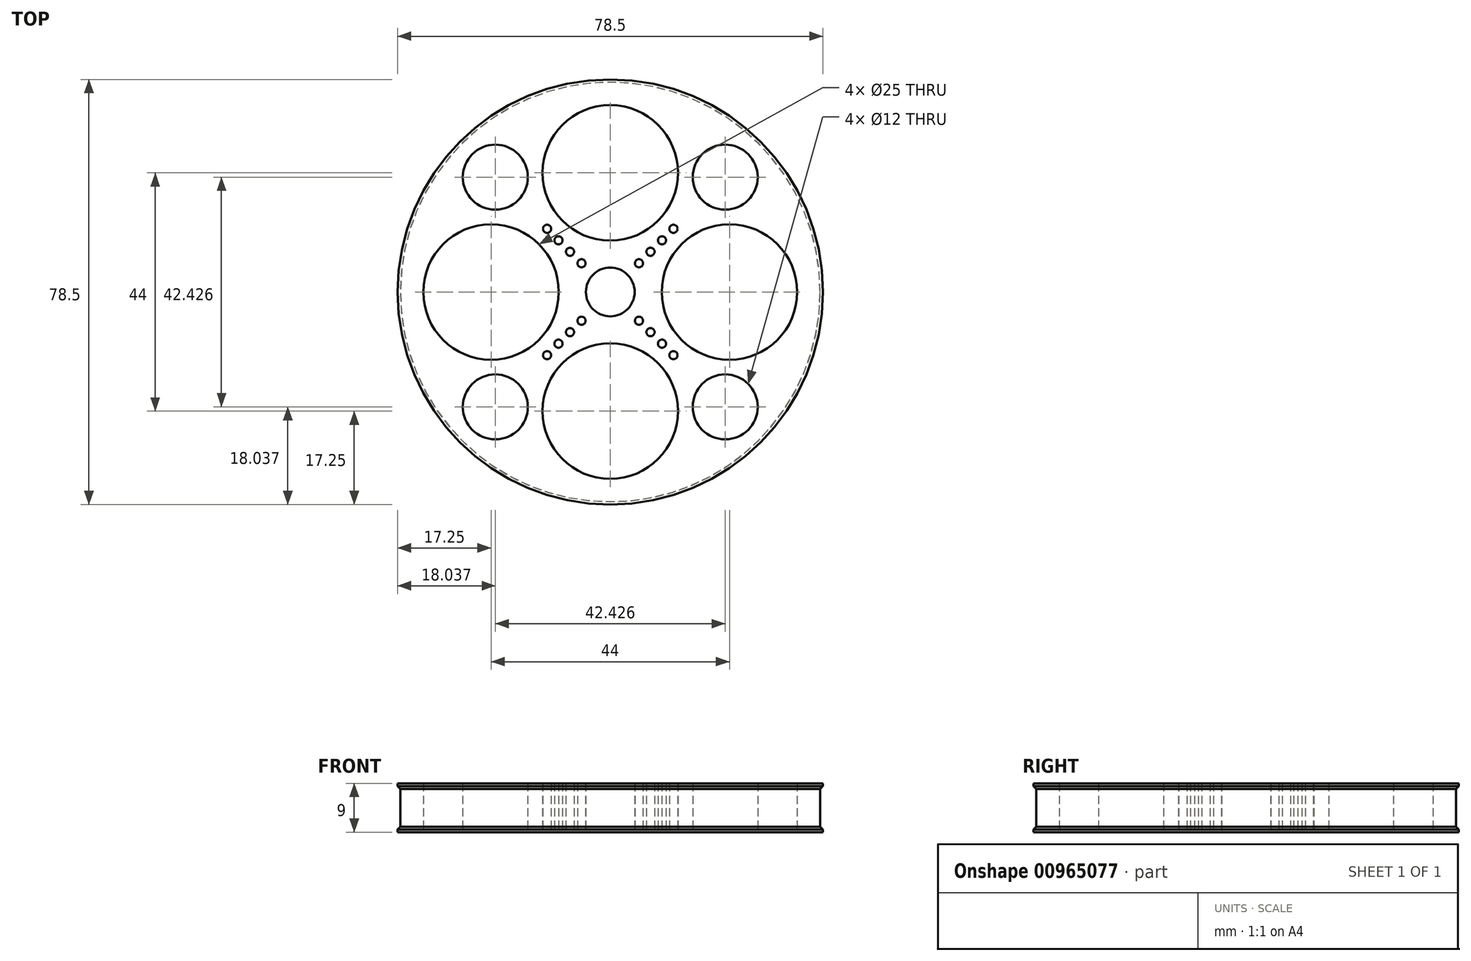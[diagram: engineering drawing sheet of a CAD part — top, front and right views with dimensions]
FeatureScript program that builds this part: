
annotation { "Feature Type Name" : "Feature", "Feature Type Description" : "" }
export const myFeature = defineFeature(function(context is Context, id is Id, definition is map)
    precondition{}
    {
        {
            var Q0;
            Q0=qCreatedBy(makeId("Top.planeOp"),FACE);
            var sketch = newSketch(context, id + "F0", { "sketchPlane" : qUnion([Q0])});
            skCircle(sketch, "E0", {"center": v(0, 0) * mm, "radius": 38.71 * mm});
            skCircle(sketch, "E1", {"center": v(0, 0) * mm, "radius": 4.5 * mm});
            skCircle(sketch, "E2", {"center": v(0, 22) * mm, "radius": 12.5 * mm});
            skCircle(sketch, "E3", {"center": v(22, 0) * mm, "radius": 12.5 * mm});
            skCircle(sketch, "E4", {"center": v(0, -22) * mm, "radius": 12.5 * mm});
            skCircle(sketch, "E5", {"center": v(-22, 0) * mm, "radius": 12.5 * mm});
            skLineSegment(sketch, "E6", {"start": v(0, 0) * mm, "end": v(36.46, 36.46) * mm, "construction": true});
            skLineSegment(sketch, "E7", {"start": v(0, 0) * mm, "end": v(-38.26, -38.26) * mm, "construction": true});
            skLineSegment(sketch, "E8", {"start": v(0, 0) * mm, "end": v(36.23, -36.23) * mm, "construction": true});
            skLineSegment(sketch, "E9", {"start": v(0, 0) * mm, "end": v(-38.7, 38.7) * mm, "construction": true});
            skCircle(sketch, "E10", {"center": v(21.21, -21.21) * mm, "radius": 6 * mm});
            skCircle(sketch, "E11", {"center": v(21.21, 21.21) * mm, "radius": 6 * mm});
            skCircle(sketch, "E12", {"center": v(-21.21, 21.21) * mm, "radius": 6 * mm});
            skCircle(sketch, "E13", {"center": v(-21.21, -21.21) * mm, "radius": 6 * mm});
            skCircle(sketch, "E14", {"center": v(5.3, 5.3) * mm, "radius": 0.75 * mm});
            skCircle(sketch, "E15", {"center": v(-5.3, -5.3) * mm, "radius": 0.75 * mm});
            skCircle(sketch, "E16", {"center": v(-5.3, 5.3) * mm, "radius": 0.75 * mm});
            skCircle(sketch, "E17", {"center": v(5.3, -5.3) * mm, "radius": 0.75 * mm});
            skCircle(sketch, "E18", {"center": v(7.42, 7.42) * mm, "radius": 0.75 * mm});
            skCircle(sketch, "E19", {"center": v(9.55, 9.55) * mm, "radius": 0.75 * mm});
            skCircle(sketch, "E20", {"center": v(11.67, 11.67) * mm, "radius": 0.75 * mm});
            skCircle(sketch, "E21", {"center": v(7.42, -7.42) * mm, "radius": 0.75 * mm});
            skCircle(sketch, "E22", {"center": v(9.55, -9.55) * mm, "radius": 0.75 * mm});
            skCircle(sketch, "E23", {"center": v(11.67, -11.67) * mm, "radius": 0.75 * mm});
            skCircle(sketch, "E24", {"center": v(-7.42, -7.42) * mm, "radius": 0.75 * mm});
            skCircle(sketch, "E25", {"center": v(-9.55, -9.55) * mm, "radius": 0.75 * mm});
            skCircle(sketch, "E26", {"center": v(-11.67, -11.67) * mm, "radius": 0.75 * mm});
            skCircle(sketch, "E27", {"center": v(-7.42, 7.42) * mm, "radius": 0.75 * mm});
            skCircle(sketch, "E28", {"center": v(-9.55, 9.55) * mm, "radius": 0.75 * mm});
            skCircle(sketch, "E29", {"center": v(-11.67, 11.67) * mm, "radius": 0.75 * mm});
            skSolve(sketch);
        }
        {
            var Q0;
            Q0=makeQuery(id+"F0.imprint","IMPRINT",FACE,{"disambiguationData":[TD([[makeQuery(id+"F0.imprint","IMPRINT",EDGE,{"derivedFrom":sQuery(id+"F0.wireOp",EDGE,"E0")}),1.0]])]});
            extrude(context, id + "F1", {"entities" : qUnion([Q0]), "depth" : 7 * mm, "offsetDistance" : 25 * mm});
        }
        {
            var Q0;
            Q0=makeQuery(id+"F1.opExtrude","CAP_FACE",FACE,{"disambiguationData":[OSD([sQuery(id+"F0.wireOp",EDGE,"E0"),sQuery(id+"F0.wireOp",EDGE,"E1"),sQuery(id+"F0.wireOp",EDGE,"E2"),sQuery(id+"F0.wireOp",EDGE,"E3"),sQuery(id+"F0.wireOp",EDGE,"E4"),sQuery(id+"F0.wireOp",EDGE,"E5")])],"isStart":false});
            var sketch = newSketch(context, id + "F2", { "sketchPlane" : qUnion([Q0])});
            skCircle(sketch, "E30", {"center": v(0, 0) * mm, "radius": 39.25 * mm});
            skSolve(sketch);
        }
        {
            var Q0;
            Q0=makeQuery(id+"F2.imprint","IMPRINT",FACE,{"disambiguationData":[TD([[makeQuery(id+"F2.imprint","IMPRINT",EDGE,{"derivedFrom":sQuery(id+"F2.wireOp",EDGE,"E30")}),1.0]])]});
            var Q1;
            Q1=makeQuery(id+"F2.imprint","IMPRINT",FACE,{"disambiguationData":[TD([[makeQuery(id+"F2.imprint","IMPRINT",EDGE,{"derivedFrom":makeQuery(id+"F1.opExtrude","CAP_EDGE",EDGE,{"disambiguationData":[OSD([sQuery(id+"F0.wireOp",EDGE,"E0")])],"isStart":false})}),1.0]])]});
            extrude(context, id + "F3", {"entities" : qUnion([Q0, Q1]), "operationType" : NewBodyOperationType.ADD, "depth" : 1 * mm, "offsetDistance" : 25 * mm});
        }
        {
            var Q0;
            Q0=makeQuery(id+"F1.opExtrude","CAP_FACE",FACE,{"disambiguationData":[OSD([sQuery(id+"F0.wireOp",EDGE,"E0"),sQuery(id+"F0.wireOp",EDGE,"E1"),sQuery(id+"F0.wireOp",EDGE,"E2"),sQuery(id+"F0.wireOp",EDGE,"E3"),sQuery(id+"F0.wireOp",EDGE,"E4"),sQuery(id+"F0.wireOp",EDGE,"E5")])],"isStart":true});
            var sketch = newSketch(context, id + "F4", { "sketchPlane" : qUnion([Q0])});
            skCircle(sketch, "E31", {"center": v(0, 0) * mm, "radius": 39.25 * mm});
            skSolve(sketch);
        }
        {
            var Q0;
            Q0=makeQuery(id+"F4.imprint","IMPRINT",FACE,{"disambiguationData":[TD([[makeQuery(id+"F4.imprint","IMPRINT",EDGE,{"derivedFrom":sQuery(id+"F4.wireOp",EDGE,"E31")}),1.0]])]});
            var Q1;
            Q1=makeQuery(id+"F4.imprint","IMPRINT",FACE,{"disambiguationData":[TD([[makeQuery(id+"F4.imprint","IMPRINT",EDGE,{"derivedFrom":makeQuery(id+"F1.opExtrude","CAP_EDGE",EDGE,{"disambiguationData":[OSD([sQuery(id+"F0.wireOp",EDGE,"E0")])],"isStart":true})}),-1.0]])]});
            extrude(context, id + "F5", {"entities" : qUnion([Q0, Q1]), "operationType" : NewBodyOperationType.ADD, "depth" : 1 * mm, "offsetDistance" : 25 * mm});
        }
        {
            var Q0;
            Q0=makeQuery(id+"F5.opExtrude","CAP_EDGE",EDGE,{"disambiguationData":[OSD([sQuery(id+"F4.wireOp",EDGE,"E31")])],"isStart":true});
            var Q1;
            Q1=makeQuery(id+"F3.opExtrude","CAP_EDGE",EDGE,{"disambiguationData":[OSD([sQuery(id+"F2.wireOp",EDGE,"E30")])],"isStart":true});
            chamfer(context, id + "F6", {"entities" : qUnion([Q0, Q1]), "width" : .5 * mm, "tangentPropagation" : true});
        }
    });
